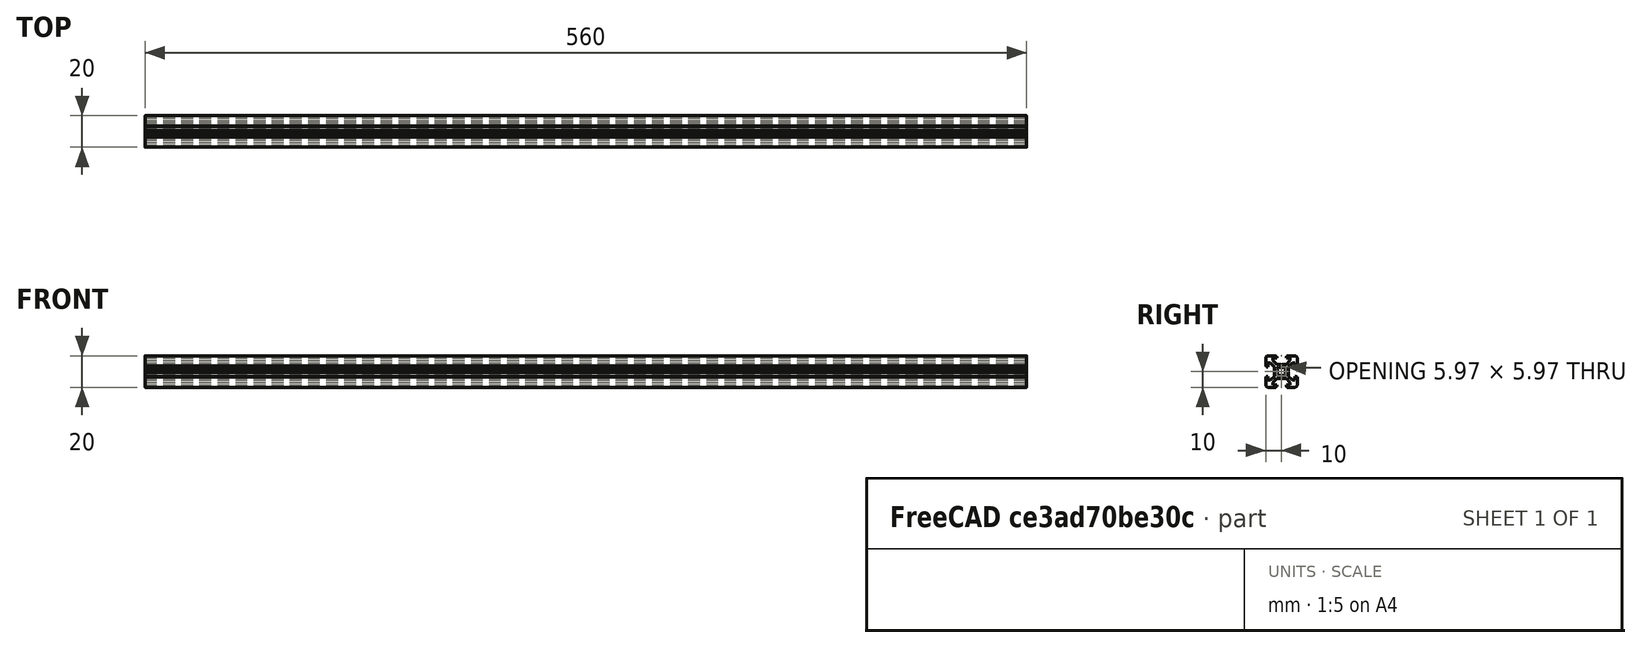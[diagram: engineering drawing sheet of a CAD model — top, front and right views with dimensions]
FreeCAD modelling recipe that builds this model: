
FCSTD DOCUMENT  (FreeCAD 0.19R)
Label: Tslot56
License: All rights reserved
LicenseURL: http://en.wikipedia.org/wiki/All_rights_reserved
objects: Sketcher::SketchObject×1, PartDesign::Pad×1, PartDesign::Body×1
note: 4 computed .brp shape members not serialized (recipe doc carries the construction recipe); baked Part::Feature solids carry a one-line shape summary decoded from their .brp

FEATURE [Sketcher::SketchObject] Sketch  label="T-Slot-Skizze"
  FullyConstrained = true
  MapMode = 5
  Placement = pos=(0,0,0) rot=(0.57735,0.57735,0.57735;2.0944rad)
  Support = -> [YZ_Plane]
  sketch-geometry (98):
    g0: LineSegment StartX=0 StartY=4.1 StartZ=0 EndX=0.65 EndY=4.5 EndZ=0
    g1: LineSegment StartX=0.65 StartY=4.5 StartZ=0 EndX=3 EndY=4.5 EndZ=0
    g2: LineSegment StartX=3 StartY=4.5 StartZ=0 EndX=5.5 EndY=7 EndZ=0
    g3: LineSegment StartX=5.5 StartY=7 StartZ=0 EndX=5.5 EndY=8.5 EndZ=0
    g4: LineSegment StartX=5.5 StartY=8.5 StartZ=0 EndX=3 EndY=8.5 EndZ=0
    g5: LineSegment StartX=3 StartY=8.5 StartZ=0 EndX=3 EndY=9.5 EndZ=0
    g6: LineSegment StartX=3 StartY=9.5 StartZ=0 EndX=3.5 EndY=9.5 EndZ=0
    g7: LineSegment StartX=3.5 StartY=9.5 StartZ=0 EndX=3.5 EndY=10 EndZ=0
    g8: LineSegment StartX=3.5 StartY=10 StartZ=0 EndX=8.5 EndY=10 EndZ=0
    g9: LineSegment StartX=10 StartY=8.5 StartZ=0 EndX=10 EndY=3.5 EndZ=0
    g10: LineSegment StartX=10 StartY=3.5 StartZ=0 EndX=9.5 EndY=3.5 EndZ=0
    g11: LineSegment StartX=9.5 StartY=3.5 StartZ=0 EndX=9.5 EndY=3 EndZ=0
    g12: LineSegment StartX=9.5 StartY=3 StartZ=0 EndX=8.5 EndY=3 EndZ=0
    g13: LineSegment StartX=8.5 StartY=3 StartZ=0 EndX=8.5 EndY=5.5 EndZ=0
    g14: LineSegment StartX=8.5 StartY=5.5 StartZ=0 EndX=7 EndY=5.5 EndZ=0
    g15: LineSegment StartX=7 StartY=5.5 StartZ=0 EndX=4.5 EndY=3 EndZ=0
    g16: LineSegment StartX=4.5 StartY=3 StartZ=0 EndX=4.5 EndY=0.65 EndZ=0
    g17: LineSegment StartX=4.5 StartY=0.65 StartZ=0 EndX=4.1 EndY=0 EndZ=0
    g18: ArcOfCircle CenterX=8.5 CenterY=8.5 CenterZ=0 NormalX=0 NormalY=0 NormalZ=1 AngleXU=0 Radius=1.5 StartAngle=0 EndAngle=1.5708
    g19: LineSegment StartX=0 StartY=-4.1 StartZ=0 EndX=0.65 EndY=-4.5 EndZ=0
    g20: LineSegment StartX=0.65 StartY=-4.5 StartZ=0 EndX=3 EndY=-4.5 EndZ=0
    g21: LineSegment StartX=3 StartY=-4.5 StartZ=0 EndX=5.5 EndY=-7 EndZ=0
    g22: LineSegment StartX=5.5 StartY=-7 StartZ=0 EndX=5.5 EndY=-8.5 EndZ=0
    g23: LineSegment StartX=5.5 StartY=-8.5 StartZ=0 EndX=3 EndY=-8.5 EndZ=0
    g24: LineSegment StartX=3 StartY=-8.5 StartZ=0 EndX=3 EndY=-9.5 EndZ=0
    g25: LineSegment StartX=3 StartY=-9.5 StartZ=0 EndX=3.5 EndY=-9.5 EndZ=0
    g26: LineSegment StartX=3.5 StartY=-9.5 StartZ=0 EndX=3.5 EndY=-10 EndZ=0
    g27: LineSegment StartX=3.5 StartY=-10 StartZ=0 EndX=8.5 EndY=-10 EndZ=0
    g28: LineSegment StartX=10 StartY=-8.5 StartZ=0 EndX=10 EndY=-3.5 EndZ=0
    g29: LineSegment StartX=10 StartY=-3.5 StartZ=0 EndX=9.5 EndY=-3.5 EndZ=0
    g30: LineSegment StartX=9.5 StartY=-3.5 StartZ=0 EndX=9.5 EndY=-3 EndZ=0
    g31: LineSegment StartX=9.5 StartY=-3 StartZ=0 EndX=8.5 EndY=-3 EndZ=0
    g32: LineSegment StartX=8.5 StartY=-3 StartZ=0 EndX=8.5 EndY=-5.5 EndZ=0
    g33: LineSegment StartX=8.5 StartY=-5.5 StartZ=0 EndX=7 EndY=-5.5 EndZ=0
    g34: LineSegment StartX=7 StartY=-5.5 StartZ=0 EndX=4.5 EndY=-3 EndZ=0
    g35: LineSegment StartX=4.5 StartY=-3 StartZ=0 EndX=4.5 EndY=-0.65 EndZ=0
    g36: ArcOfCircle CenterX=8.5 CenterY=-8.5 CenterZ=0 NormalX=0 NormalY=0 NormalZ=1 AngleXU=0 Radius=1.5 StartAngle=4.71239 EndAngle=6.28319
    g37: LineSegment StartX=4.5 StartY=-0.65 StartZ=0 EndX=4.1 EndY=0 EndZ=0
    g38: LineSegment StartX=0 StartY=-4.1 StartZ=0 EndX=-0.65 EndY=-4.5 EndZ=0
    g39: LineSegment StartX=-0.65 StartY=-4.5 StartZ=0 EndX=-3 EndY=-4.5 EndZ=0
    g40: LineSegment StartX=-3 StartY=-4.5 StartZ=0 EndX=-5.5 EndY=-7 EndZ=0
    g41: LineSegment StartX=-5.5 StartY=-7 StartZ=0 EndX=-5.5 EndY=-8.5 EndZ=0
    g42: LineSegment StartX=-5.5 StartY=-8.5 StartZ=0 EndX=-3 EndY=-8.5 EndZ=0
    g43: LineSegment StartX=-3 StartY=-8.5 StartZ=0 EndX=-3 EndY=-9.5 EndZ=0
    g44: LineSegment StartX=-3 StartY=-9.5 StartZ=0 EndX=-3.5 EndY=-9.5 EndZ=0
    g45: LineSegment StartX=-3.5 StartY=-9.5 StartZ=0 EndX=-3.5 EndY=-10 EndZ=0
    g46: LineSegment StartX=-3.5 StartY=-10 StartZ=0 EndX=-8.5 EndY=-10 EndZ=0
    g47: LineSegment StartX=-10 StartY=-8.5 StartZ=0 EndX=-10 EndY=-3.5 EndZ=0
    g48: LineSegment StartX=-10 StartY=-3.5 StartZ=0 EndX=-9.5 EndY=-3.5 EndZ=0
    g49: LineSegment StartX=-9.5 StartY=-3.5 StartZ=0 EndX=-9.5 EndY=-3 EndZ=0
    g50: LineSegment StartX=-9.5 StartY=-3 StartZ=0 EndX=-8.5 EndY=-3 EndZ=0
    g51: LineSegment StartX=-8.5 StartY=-3 StartZ=0 EndX=-8.5 EndY=-5.5 EndZ=0
    g52: LineSegment StartX=-8.5 StartY=-5.5 StartZ=0 EndX=-7 EndY=-5.5 EndZ=0
    g53: LineSegment StartX=-7 StartY=-5.5 StartZ=0 EndX=-4.5 EndY=-3 EndZ=0
    g54: LineSegment StartX=-4.5 StartY=-3 StartZ=0 EndX=-4.5 EndY=-0.65 EndZ=0
    g55: ArcOfCircle CenterX=-8.5 CenterY=-8.5 CenterZ=0 NormalX=0 NormalY=0 NormalZ=1 AngleXU=0 Radius=1.5 StartAngle=3.14159 EndAngle=4.71239
    g56: LineSegment StartX=-4.5 StartY=-0.65 StartZ=0 EndX=-4.1 EndY=0 EndZ=0
    g57: LineSegment StartX=-0.65 StartY=4.5 StartZ=0 EndX=-3 EndY=4.5 EndZ=0
    g58: LineSegment StartX=-3 StartY=4.5 StartZ=0 EndX=-5.5 EndY=7 EndZ=0
    g59: LineSegment StartX=-5.5 StartY=7 StartZ=0 EndX=-5.5 EndY=8.5 EndZ=0
    g60: LineSegment StartX=-5.5 StartY=8.5 StartZ=0 EndX=-3 EndY=8.5 EndZ=0
    g61: LineSegment StartX=-3 StartY=8.5 StartZ=0 EndX=-3 EndY=9.5 EndZ=0
    g62: LineSegment StartX=-3 StartY=9.5 StartZ=0 EndX=-3.5 EndY=9.5 EndZ=0
    g63: LineSegment StartX=-3.5 StartY=9.5 StartZ=0 EndX=-3.5 EndY=10 EndZ=0
    g64: LineSegment StartX=-3.5 StartY=10 StartZ=0 EndX=-8.5 EndY=10 EndZ=0
    g65: LineSegment StartX=-10 StartY=8.5 StartZ=0 EndX=-10 EndY=3.5 EndZ=0
    g66: LineSegment StartX=-10 StartY=3.5 StartZ=0 EndX=-9.5 EndY=3.5 EndZ=0
    g67: LineSegment StartX=-9.5 StartY=3.5 StartZ=0 EndX=-9.5 EndY=3 EndZ=0
    g68: LineSegment StartX=-9.5 StartY=3 StartZ=0 EndX=-8.5 EndY=3 EndZ=0
    g69: LineSegment StartX=-8.5 StartY=3 StartZ=0 EndX=-8.5 EndY=5.5 EndZ=0
    g70: LineSegment StartX=-8.5 StartY=5.5 StartZ=0 EndX=-7 EndY=5.5 EndZ=0
    g71: LineSegment StartX=-7 StartY=5.5 StartZ=0 EndX=-4.5 EndY=3 EndZ=0
    g72: LineSegment StartX=-4.5 StartY=3 StartZ=0 EndX=-4.5 EndY=0.65 EndZ=0
    g73: ArcOfCircle CenterX=-8.5 CenterY=8.5 CenterZ=0 NormalX=0 NormalY=0 NormalZ=1 AngleXU=0 Radius=1.5 StartAngle=1.5708 EndAngle=3.14159
    g74: LineSegment StartX=-4.5 StartY=0.65 StartZ=0 EndX=-4.1 EndY=0 EndZ=0
    g75: LineSegment StartX=0 StartY=4.1 StartZ=0 EndX=-0.65 EndY=4.5 EndZ=0
    g76: Circle CenterX=0 CenterY=0 CenterZ=0 NormalX=0 NormalY=0 NormalZ=1 AngleXU=0 Radius=3.55
    g77: Circle CenterX=0 CenterY=0 CenterZ=0 NormalX=0 NormalY=0 NormalZ=1 AngleXU=0 Radius=2.75
    g78: LineSegment StartX=1.3405 StartY=2.40116 StartZ=0 EndX=1.92324 EndY=2.9839 EndZ=0
    g79: LineSegment StartX=1.92324 StartY=2.9839 StartZ=0 EndX=2.9839 EndY=1.92324 EndZ=0
    g80: LineSegment StartX=2.9839 StartY=1.92324 StartZ=0 EndX=2.40116 EndY=1.3405 EndZ=0
    g81: ArcOfCircle CenterX=0 CenterY=0 CenterZ=0 NormalX=0 NormalY=0 NormalZ=1 AngleXU=0 Radius=2.75 StartAngle=0 EndAngle=0.509172
    g82: ArcOfCircle CenterX=0 CenterY=0 CenterZ=0 NormalX=0 NormalY=0 NormalZ=1 AngleXU=0 Radius=2.75 StartAngle=1.06162 EndAngle=1.5708
    g83: LineSegment StartX=-1.3405 StartY=2.40116 StartZ=0 EndX=-1.92324 EndY=2.9839 EndZ=0
    g84: LineSegment StartX=-1.92324 StartY=2.9839 StartZ=0 EndX=-2.9839 EndY=1.92324 EndZ=0
    g85: LineSegment StartX=-2.9839 StartY=1.92324 StartZ=0 EndX=-2.40116 EndY=1.3405 EndZ=0
    g86: ArcOfCircle CenterX=-1.3e-15 CenterY=6e-16 CenterZ=0 NormalX=0 NormalY=0 NormalZ=1 AngleXU=0 Radius=2.75 StartAngle=2.63242 EndAngle=3.14159
    g87: ArcOfCircle CenterX=-1.3e-15 CenterY=6e-16 CenterZ=0 NormalX=0 NormalY=0 NormalZ=1 AngleXU=0 Radius=2.75 StartAngle=1.5708 EndAngle=2.07997
    g88: LineSegment StartX=-1.34051 StartY=-2.40115 StartZ=0 EndX=-1.92325 EndY=-2.98389 EndZ=0
    g89: LineSegment StartX=-1.92325 StartY=-2.98389 StartZ=0 EndX=-2.9839 EndY=-1.92323 EndZ=0
    g90: LineSegment StartX=-2.9839 StartY=-1.92323 StartZ=0 EndX=-2.40116 EndY=-1.34049 EndZ=0
    g91: ArcOfCircle CenterX=-3e-16 CenterY=2e-16 CenterZ=0 NormalX=0 NormalY=0 NormalZ=1 AngleXU=0 Radius=2.75 StartAngle=3.14159 EndAngle=3.65076
    g92: ArcOfCircle CenterX=-3e-16 CenterY=2e-16 CenterZ=0 NormalX=0 NormalY=0 NormalZ=1 AngleXU=0 Radius=2.75 StartAngle=4.20321 EndAngle=4.71239
    g93: LineSegment StartX=1.34051 StartY=-2.40115 StartZ=0 EndX=1.92325 EndY=-2.98389 EndZ=0
    g94: LineSegment StartX=1.92325 StartY=-2.98389 StartZ=0 EndX=2.9839 EndY=-1.92323 EndZ=0
    g95: LineSegment StartX=2.9839 StartY=-1.92323 StartZ=0 EndX=2.40116 EndY=-1.34049 EndZ=0
    g96: ArcOfCircle CenterX=3e-16 CenterY=2e-16 CenterZ=0 NormalX=0 NormalY=0 NormalZ=1 AngleXU=0 Radius=2.75 StartAngle=4.71239 EndAngle=5.22156
    g97: ArcOfCircle CenterX=3e-16 CenterY=2e-16 CenterZ=0 NormalX=0 NormalY=0 NormalZ=1 AngleXU=0 Radius=2.75 StartAngle=5.77402 EndAngle=6.28319
  constraints (291):
    c: PointOnObject(g0,g-2)
    c: Coincident(g0,g1)
    c: Horizontal(g1)
    c: Coincident(g1,g2)
    c: Coincident(g2,g3)
    c: Vertical(g3)
    c: Coincident(g3,g4)
    c: Horizontal(g4)
    c: Coincident(g4,g5)
    c: Vertical(g5)
    c: Coincident(g5,g6)
    c: Horizontal(g6)
    c: Coincident(g6,g7)
    c: Coincident(g7,g8)
    c: Horizontal(g8)
    c: Vertical(g7)
    c: DistanceX(g-1,g5) = 3
    c: DistanceY(g4,g7) = 1.5
    c: DistanceY(g0,g7) = 5.5
    c: DistanceY(g3,g3) = 1.5
    c: DistanceY(g4,g5) = 1
    c: DistanceX(g-1,g1) = 3
    c: DistanceX(g-1,g7) = 3.5
    c: DistanceX(g0,g0) = 0.65
    c: DistanceY(g0,g0) = 0.4
    c: DistanceX(g-1,g3) = 5.5
    c: Vertical(g9)
    c: Coincident(g9,g10)
    c: Coincident(g10,g11)
    c: Coincident(g11,g12)
    c: Coincident(g12,g13)
    c: Vertical(g13)
    c: Coincident(g13,g14)
    c: Horizontal(g14)
    c: Coincident(g14,g15)
    c: Coincident(g15,g16)
    c: Vertical(g16)
    c: Coincident(g16,g17)
    c: PointOnObject(g17,g-1)
    c: Horizontal(g10)
    c: Horizontal(g12)
    c: Vertical(g11)
    c: Equal(g17,g0)
    c: Equal(g1,g16)
    c: Equal(g15,g2)
    c: Equal(g3,g14)
    c: Equal(g13,g4)
    c: Equal(g12,g5)
    c: Parallel(g15,g2)
    c: Equal(g11,g6)
    c: Equal(g10,g7)
    c: Equal(g9,g8)
    c: Tangent(g8,g18) = 1.5708
    c: Tangent(g9,g18) = 1.5708
    c: Radius(g18) = 1.5
    c: DistanceY(g-1,g8) = 10
    c: DistanceX(g-1,g9) = 10
    c: Coincident(g19,g20)
    c: Horizontal(g20)
    c: Coincident(g20,g21)
    c: Coincident(g21,g22)
    c: Vertical(g22)
    c: Coincident(g22,g23)
    c: Horizontal(g23)
    c: Coincident(g23,g24)
    c: Vertical(g24)
    c: Coincident(g24,g25)
    c: Horizontal(g25)
    c: Coincident(g25,g26)
    c: Coincident(g26,g27)
    c: Horizontal(g27)
    c: Vertical(g26)
    c: Vertical(g28)
    c: Coincident(g28,g29)
    c: Coincident(g29,g30)
    c: Coincident(g30,g31)
    c: Coincident(g31,g32)
    c: Vertical(g32)
    c: Coincident(g32,g33)
    c: Horizontal(g33)
    c: Coincident(g33,g34)
    c: Coincident(g34,g35)
    c: Vertical(g35)
    c: Coincident(g35,g37)
    c: Horizontal(g29)
    c: Horizontal(g31)
    c: Vertical(g30)
    c: Equal(g37,g19)
    c: Equal(g20,g35)
    c: Equal(g34,g21)
    c: Equal(g22,g33)
    c: Equal(g32,g23)
    c: Equal(g31,g24)
    c: Parallel(g34,g21)
    c: Equal(g30,g25)
    c: Equal(g29,g26)
    c: Equal(g28,g27)
    c: Tangent(g27,g36) = -1.5708
    c: Tangent(g28,g36) = -1.5708
    c: Radius(g36) = 1.5
    c: Equal(g9,g28)
    c: Equal(g12,g31)
    c: DistanceX(g-1,g28) = 10
    c: DistanceY(g27,g-1) = 10
    c: DistanceY(g30,g-1) = 3
    c: Equal(g33,g14)
    c: Equal(g35,g16)
    c: Equal(g17,g37)
    c: Coincident(g37,g17)
    c: Equal(g15,g34)
    c: PointOnObject(g19,g-2)
    c: DistanceY(g34,g-1) = 3
    c: DistanceX(g-1,g20) = 3
    c: Coincident(g38,g39)
    c: Horizontal(g39)
    c: Coincident(g39,g40)
    c: Coincident(g40,g41)
    c: Vertical(g41)
    c: Coincident(g41,g42)
    c: Horizontal(g42)
    c: Coincident(g42,g43)
    c: Vertical(g43)
    c: Coincident(g43,g44)
    c: Horizontal(g44)
    c: Coincident(g44,g45)
    c: Coincident(g45,g46)
    c: Horizontal(g46)
    c: Vertical(g45)
    c: Vertical(g47)
    c: Coincident(g47,g48)
    c: Coincident(g48,g49)
    c: Coincident(g49,g50)
    c: Coincident(g50,g51)
    c: Vertical(g51)
    c: Coincident(g51,g52)
    c: Horizontal(g52)
    c: Coincident(g52,g53)
    c: Coincident(g53,g54)
    c: Vertical(g54)
    c: Coincident(g54,g56)
    c: Horizontal(g48)
    c: Horizontal(g50)
    c: Vertical(g49)
    c: Equal(g39,g54)
    c: Equal(g53,g40)
    c: Equal(g41,g52)
    c: Equal(g51,g42)
    c: Equal(g50,g43)
    c: Parallel(g53,g40)
    c: Equal(g49,g44)
    c: Equal(g48,g45)
    c: Equal(g47,g46)
    c: Tangent(g46,g55) = 1.5708
    c: Tangent(g47,g55) = 1.5708
    c: Radius(g55) = 1.5
    c: Coincident(g38,g19)
    c: DistanceX(g39,g-1) = 3
    c: DistanceX(g38,g19) = 0.65
    c: DistanceY(g38,g19) = 0.4
    c: PointOnObject(g56,g-1)
    c: Equal(g56,g38)
    c: DistanceY(g53,g-1) = 3
    c: Equal(g22,g41)
    c: Equal(g42,g23)
    c: Equal(g24,g43)
    c: Equal(g25,g44)
    c: Equal(g26,g45)
    c: DistanceY(g46,g-1) = 10
    c: DistanceX(g47,g-1) = 10
    c: Coincident(g75,g57)
    c: Horizontal(g57)
    c: Coincident(g57,g58)
    c: Coincident(g58,g59)
    c: Vertical(g59)
    c: Coincident(g59,g60)
    c: Horizontal(g60)
    c: Coincident(g60,g61)
    c: Vertical(g61)
    c: Coincident(g61,g62)
    c: Horizontal(g62)
    c: Coincident(g62,g63)
    c: Coincident(g63,g64)
    c: Horizontal(g64)
    c: Vertical(g63)
    c: Vertical(g65)
    c: Coincident(g65,g66)
    c: Coincident(g66,g67)
    c: Coincident(g67,g68)
    c: Coincident(g68,g69)
    c: Vertical(g69)
    c: Coincident(g69,g70)
    c: Horizontal(g70)
    c: Coincident(g70,g71)
    c: Coincident(g71,g72)
    c: Vertical(g72)
    c: Coincident(g72,g74)
    c: Horizontal(g66)
    c: Horizontal(g68)
    c: Vertical(g67)
    c: Equal(g57,g72)
    c: Equal(g71,g58)
    c: Equal(g59,g70)
    c: Equal(g69,g60)
    c: Equal(g68,g61)
    c: Parallel(g71,g58)
    c: Equal(g67,g62)
    c: Equal(g66,g63)
    c: Equal(g65,g64)
    c: Tangent(g64,g73) = -1.5708
    c: Tangent(g65,g73) = -1.5708
    c: Radius(g73) = 1.5
    c: Equal(g74,g75)
    c: Coincident(g56,g74)
    c: Coincident(g0,g75)
    c: Equal(g0,g75)
    c: Equal(g1,g57)
    c: Equal(g2,g58)
    c: Equal(g3,g59)
    c: Equal(g4,g60)
    c: Equal(g5,g61)
    c: Equal(g6,g62)
    c: Equal(g7,g63)
    c: Equal(g8,g64)
    c: DistanceX(g65,g-1) = 10
    c: Coincident(g76,g-1)
    c: Coincident(g77,g-1)
    c: Radius(g76) = 3.55
    c: Radius(g77) = 2.75
    c: PointOnObject(g78,g77)
    c: PointOnObject(g78,g76)
    c: Coincident(g78,g79)
    c: PointOnObject(g79,g76)
    c: Coincident(g79,g80)
    c: PointOnObject(g80,g77)
    c: Coincident(g81,g-1)
    c: Coincident(g81,g80)
    c: Coincident(g82,g81)
    c: Coincident(g82,g78)
    c: Parallel(g78,g80)
    c: Parallel(g78,g2)
    c: Distance(g79) = 1.5
    c: Distance(g78,g80) = 1.5
    c: PointOnObject(g82,g-2)
    c: PointOnObject(g81,g-1)
    c: Coincident(g83,g84)
    c: Coincident(g84,g85)
    c: Coincident(g86,g85)
    c: Coincident(g87,g86)
    c: Coincident(g87,g83)
    c: Parallel(g83,g85)
    c: Distance(g84) = 1.5
    c: Distance(g83,g85) = 1.5
    c: Coincident(g82,g87)
    c: PointOnObject(g86,g-1)
    c: PointOnObject(g83,g76)
    c: PointOnObject(g83,g77)
    c: PointOnObject(g85,g77)
    c: PointOnObject(g84,g76)
    c: PointOnObject(g86,g77)
    c: Parallel(g85,g71)
    c: Coincident(g88,g89)
    c: Coincident(g89,g90)
    c: Coincident(g91,g90)
    c: Coincident(g92,g91)
    c: Coincident(g92,g88)
    c: Parallel(g88,g90)
    c: Distance(g89) = 1.5
    c: Distance(g88,g90) = 1.5
    c: PointOnObject(g88,g77)
    c: PointOnObject(g90,g77)
    c: Coincident(g86,g91)
    c: PointOnObject(g89,g76)
    c: PointOnObject(g88,g76)
    c: PointOnObject(g92,g-2)
    c: PointOnObject(g92,g77)
    c: Parallel(g88,g40)
    c: Coincident(g93,g94)
    c: Coincident(g94,g95)
    c: Coincident(g97,g95)
    c: Coincident(g96,g97)
    c: Coincident(g96,g93)
    c: Parallel(g93,g95)
    c: Distance(g94) = 1.5
    c: Distance(g93,g95) = 1.5
    c: Coincident(g81,g97)
    c: Coincident(g92,g96)
    c: PointOnObject(g93,g77)
    c: PointOnObject(g95,g77)
    c: PointOnObject(g94,g76)
    c: PointOnObject(g93,g76)
    c: Parallel(g93,g21)
FEATURE [PartDesign::Pad] Pad  label="T-Slot-Element"
  Direction = (1,1,1)
  Length = 560
  Length2 = 100
  Placement = pos=(0,0,0) rot=(0.57735,0.57735,0.57735;2.0944rad)
  Profile = -> Sketch
  Type = 0
FEATURE [PartDesign::Body] Body  label="T-Slot-Profil 20x20"
  Group = -> [Sketch,Pad]
  Origin = -> Origin
  Tip = -> Pad
